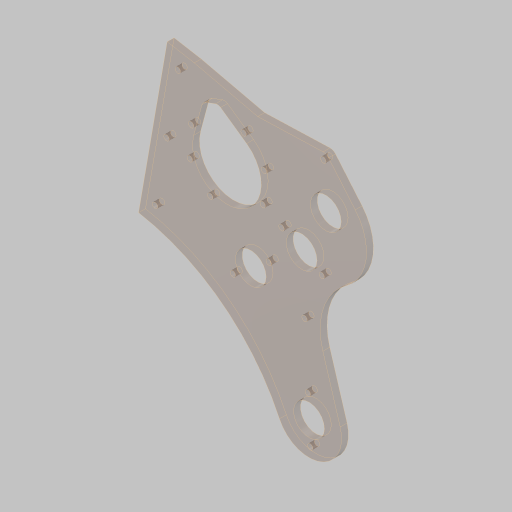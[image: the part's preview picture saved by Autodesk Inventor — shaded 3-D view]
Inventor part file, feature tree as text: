
AUTODESK INVENTOR PART (.ipt)
format: ipt  version: 2023.5 (Build 275446000, 446)  size: 313,856 bytes
history: native  units: in
note: dims shown in document units (in); Inventor stores cm internally (conversion verified against a paired STEP export)
features: sketch x5, extrude x3, hole x3, projected_geometry x3, fillet x1
ambient origin geometry x8: Origin, YZ Plane, XZ Plane, XY Plane, X Axis, Y Axis, Z Axis, Center Point
bodies: Solid1 (feature_tree)
feature tree (15):
  sketch  "Sketch1"  dims[d3=45.0deg d4=0.0in]
  extrude  "Extrusion1"  TaperAngle=0.0deg  [1 undecoded]
  hole  "Hole1"  [1 undecoded]
  hole  "Hole2"  [1 undecoded]
  extrude  "Extrusion3"  Depth=4.5in
  fillet  "Fillet2"  Radius=0.625in
  extrude  "Extrusion4"  Depth=0.25in
  hole  "Hole3"  [1 undecoded]
  sketch  "Sketch2"  dims[d7=4.0in d8=4.0in]
  projected_geometry  "Projected Loop1"
  sketch  "Sketch4"  dims[d9=1.123in d10=4.0in]
  projected_geometry  "Projected Loop2"
  sketch  "Sketch5"  dims[d11=4.5in d12=4.5in d13=0.625in]
  sketch  "Sketch6"  dims[d14=0.625in d15=5.181in d16=1.128in d17=5.181in d18=1.8765in d19=1.8765in d22=1.0in d23=6.0in d26=10.5532in d27=2.5in d30=8.0in d31=0.0687in d32=0.75in d33=4.75in d34=1.375in d35=0.75in d36=0.25in d38=2.3622in d40=360.0deg d44=0.375in d45=0.25in d46=0.0in d47=0.201in d48=0.75in d49=0.37in d50=0.25in d51=90.0deg d52=1.0in d53=0.8108in d55=0.5497in d56=0.3in d57=0.25in d58=2.256in d59=2.5in d60=2.9555in d61=2.35in d62=0.3779in d65=2.0in d66=2.3622in d68=360.0deg d70=1.625in d71=60.0deg d72=1.655in d73=0.201in d74=0.75in d75=0.385in d76=0.25in d77=0.5635in d78=1.0in d79=0.8108in d86=1.5748in d88=360.0deg d91=1.5748in d93=360.0deg d95=45.0deg d96=1.75in d98=0.8589in d99=0.0in d100=0.0in d101=0.2in d102=1.75in d103=5.75in d104=0.375in d105=0.5in d106=15.0deg d107=0.25in d108=0.0in d109=0.201in d110=0.75in d111=0.385in d112=0.25in d113=0.5635in d114=1.0in d115=0.8108in]
  projected_geometry  "Projected Loop3"
note: 4 required parameter values undecoded (feature->parameter linkage not recoverable at this tier; creation-order binding heuristic only, values carry confidence <= 0.55)
